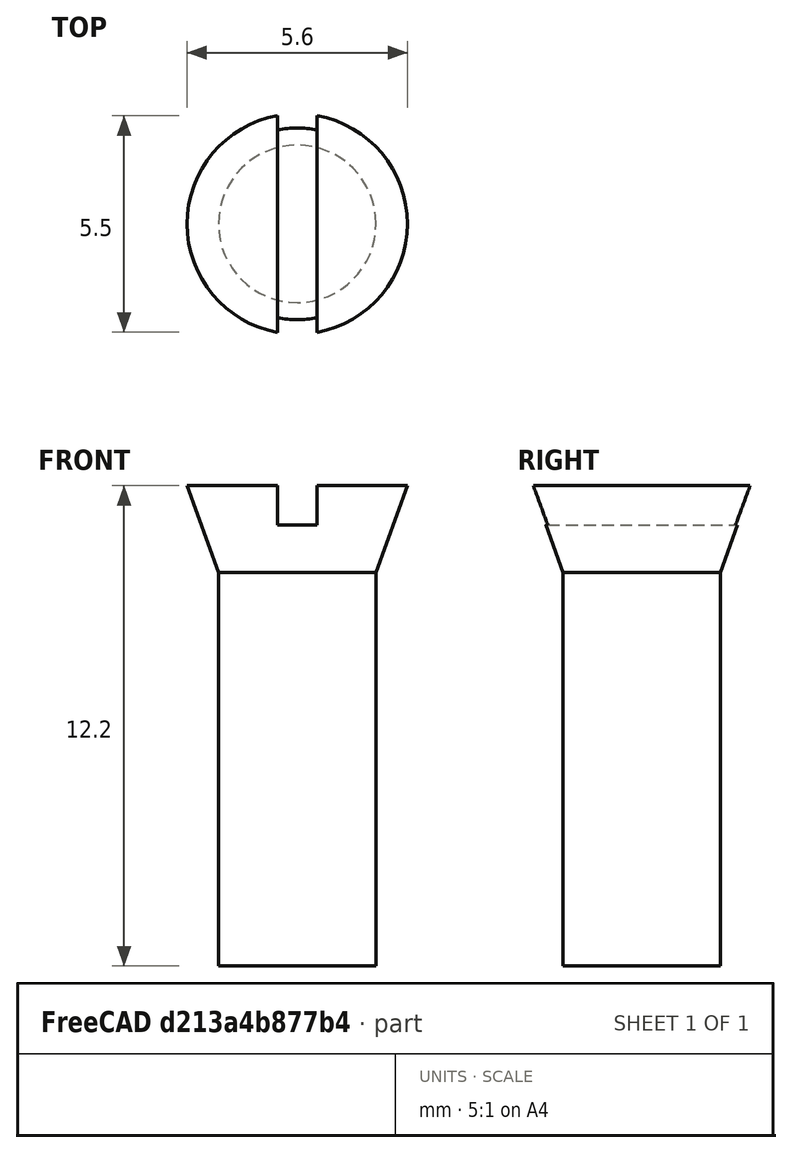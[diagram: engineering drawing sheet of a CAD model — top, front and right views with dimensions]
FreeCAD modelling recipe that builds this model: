
FCSTD DOCUMENT  (FreeCAD 1.0R39319 (Git))
Label: ojt1_t14r01_screw
License: All rights reserved
LicenseURL: https://en.wikipedia.org/wiki/All_rights_reserved
objects: Part::Cylinder×1, Part::Cone×1, Part::Box×1, Part::Cut×1
note: 4 computed .brp shape members not serialized (recipe doc carries the construction recipe); baked Part::Feature solids carry a one-line shape summary decoded from their .brp

FEATURE [Part::Cylinder] Cylinder  label="Cilindre"
  Angle = 360
  AttacherType = Attacher::AttachEngine3D
  FirstAngle = 0
  Height = 10
  Radius = 2
  SecondAngle = 0
FEATURE [Part::Cone] Cone  label="Con"
  Angle = 360
  AttacherType = Attacher::AttachEngine3D
  Height = 2.2
  Placement = pos=(0,0,10) rot=(0,0,1;0rad)
  Radius1 = 2
  Radius2 = 2.8
FEATURE [Part::Box] Box  label="Cub"
  AttacherType = Attacher::AttachEngine3D
  Height = 1
  Length = 1
  Placement = pos=(-0.5,-2.8,11.2) rot=(0,0,1;0rad)
  Width = 5.6
FEATURE [Part::Cut] Cut
  Base = -> Cone
  Refine = true
  Tool = -> Box
